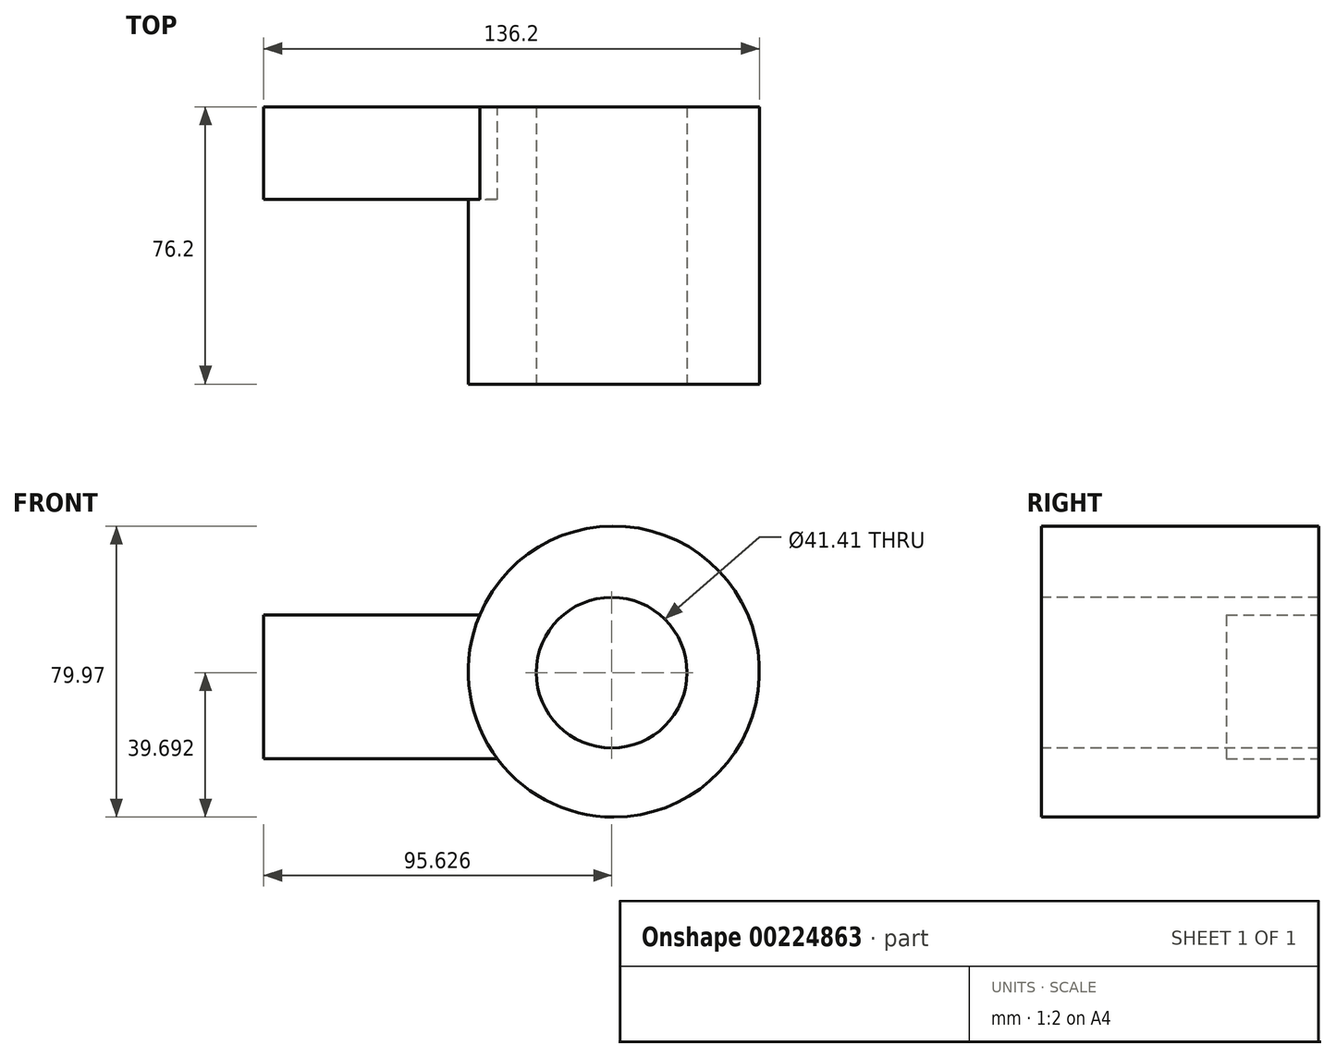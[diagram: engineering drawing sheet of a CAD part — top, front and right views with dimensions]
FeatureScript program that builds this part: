
annotation { "Feature Type Name" : "Feature", "Feature Type Description" : "" }
export const myFeature = defineFeature(function(context is Context, id is Id, definition is map)
    precondition{}
    {
        {
            var Q0;
            Q0=qCreatedBy(makeId("Front.planeOp"),FACE);
            var sketch = newSketch(context, id + "F0", { "sketchPlane" : qUnion([Q0])});
            skCircle(sketch, "E0", {"center": v(40.37, 4.53) * mm, "radius": 39.99 * mm});
            skSolve(sketch);
        }
        {
            var Q0;
            Q0=makeQuery(id+"F0.imprint","IMPRINT",FACE,{"disambiguationData":[TD([[makeQuery(id+"F0.imprint","IMPRINT",EDGE,{"derivedFrom":sQuery(id+"F0.wireOp",EDGE,"E0")}),1.0]])]});
            extrude(context, id + "F1", {"entities" : qUnion([Q0]), "depth" : 25.4 * mm});
        }
        {
            var Q0;
            Q0=makeQuery(id+"F1.opExtrude","CAP_FACE",FACE,{"disambiguationData":[OSD([sQuery(id+"F0.wireOp",EDGE,"E0")])],"isStart":false});
            extrude(context, id + "F2", {"entities" : qUnion([Q0]), "operationType" : NewBodyOperationType.ADD, "depth" : 50.8 * mm});
        }
        {
            var Q0;
            Q0=makeQuery(id+"F2.opExtrude","CAP_FACE",FACE,{"disambiguationData":[OSD([sQuery(id+"F0.wireOp",EDGE,"E0")])],"isStart":false});
            var sketch = newSketch(context, id + "F3", { "sketchPlane" : qUnion([Q0])});
            skCircle(sketch, "E1", {"center": v(39.79, 4.24) * mm, "radius": 20.7 * mm});
            skSolve(sketch);
        }
        {
            var Q0;
            Q0=makeQuery(id+"F3.imprint","IMPRINT",FACE,{"disambiguationData":[TD([[makeQuery(id+"F3.imprint","IMPRINT",EDGE,{"derivedFrom":sQuery(id+"F3.wireOp",EDGE,"E1")}),1.0]])]});
            extrude(context, id + "F4", {"entities" : qUnion([Q0]), "operationType" : NewBodyOperationType.REMOVE, "endBound" : BoundingType.THROUGH_ALL, "oppositeDirection" : true, "depth" : 25.4 * mm});
        }
        {
            var Q0;
            Q0=qCreatedBy(makeId("Front.planeOp"),FACE);
            var sketch = newSketch(context, id + "F5", { "sketchPlane" : qUnion([Q0])});
            skLineSegment(sketch, "E2.bottom", {"start": v(10.56, 20.04) * mm, "end": v(-55.84, 20.04) * mm});
            skLineSegment(sketch, "E2.top", {"start": v(10.56, -19.45) * mm, "end": v(-55.84, -19.45) * mm});
            skLineSegment(sketch, "E2.left", {"start": v(10.56, 20.04) * mm, "end": v(10.56, -19.45) * mm});
            skLineSegment(sketch, "E2.right", {"start": v(-55.84, 20.04) * mm, "end": v(-55.84, -19.45) * mm});
            skSolve(sketch);
        }
        {
            var Q0;
            Q0=makeQuery(id+"F5.imprint","IMPRINT",FACE,{"disambiguationData":[TD([[makeQuery(id+"F5.imprint","IMPRINT",EDGE,{"derivedFrom":sQuery(id+"F5.wireOp",EDGE,"E2.bottom")}),1.0]])]});
            extrude(context, id + "F6", {"entities" : qUnion([Q0]), "operationType" : NewBodyOperationType.ADD, "depth" : 25.4 * mm});
        }
    });
